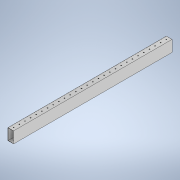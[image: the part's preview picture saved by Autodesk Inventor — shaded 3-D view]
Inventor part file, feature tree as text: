
AUTODESK INVENTOR PART (.ipt)
format: ipt  version: 2020 (Build 240168000, 168)  size: 182,272 bytes
history: native  units: in
note: dims shown in document units (in); Inventor stores cm internally (conversion verified against a paired STEP export)
features: extrude x2, sketch x2
ambient origin geometry x8: Origin, YZ Plane, XZ Plane, XY Plane, X Axis, Y Axis, Z Axis, Center Point
bodies: Solid1 (feature_tree)
feature tree (4):
  extrude  "Extrusion1"  Depth=2.0in
  extrude  "Extrusion2"  Depth=28.0in TaperAngle=0.0deg
  sketch  "Sketch1"  dims[d0=1.0in d1=2.0in]
  sketch  "Sketch2"  dims[d2=0.04in d3=28.0in d4=0.0in d5=0.1562in d6=0.5in d7=0.5in d8=11.4173in d10=1.0in d11=0.3937in d13=1.0in d15=3.0in d16=0.0in]
